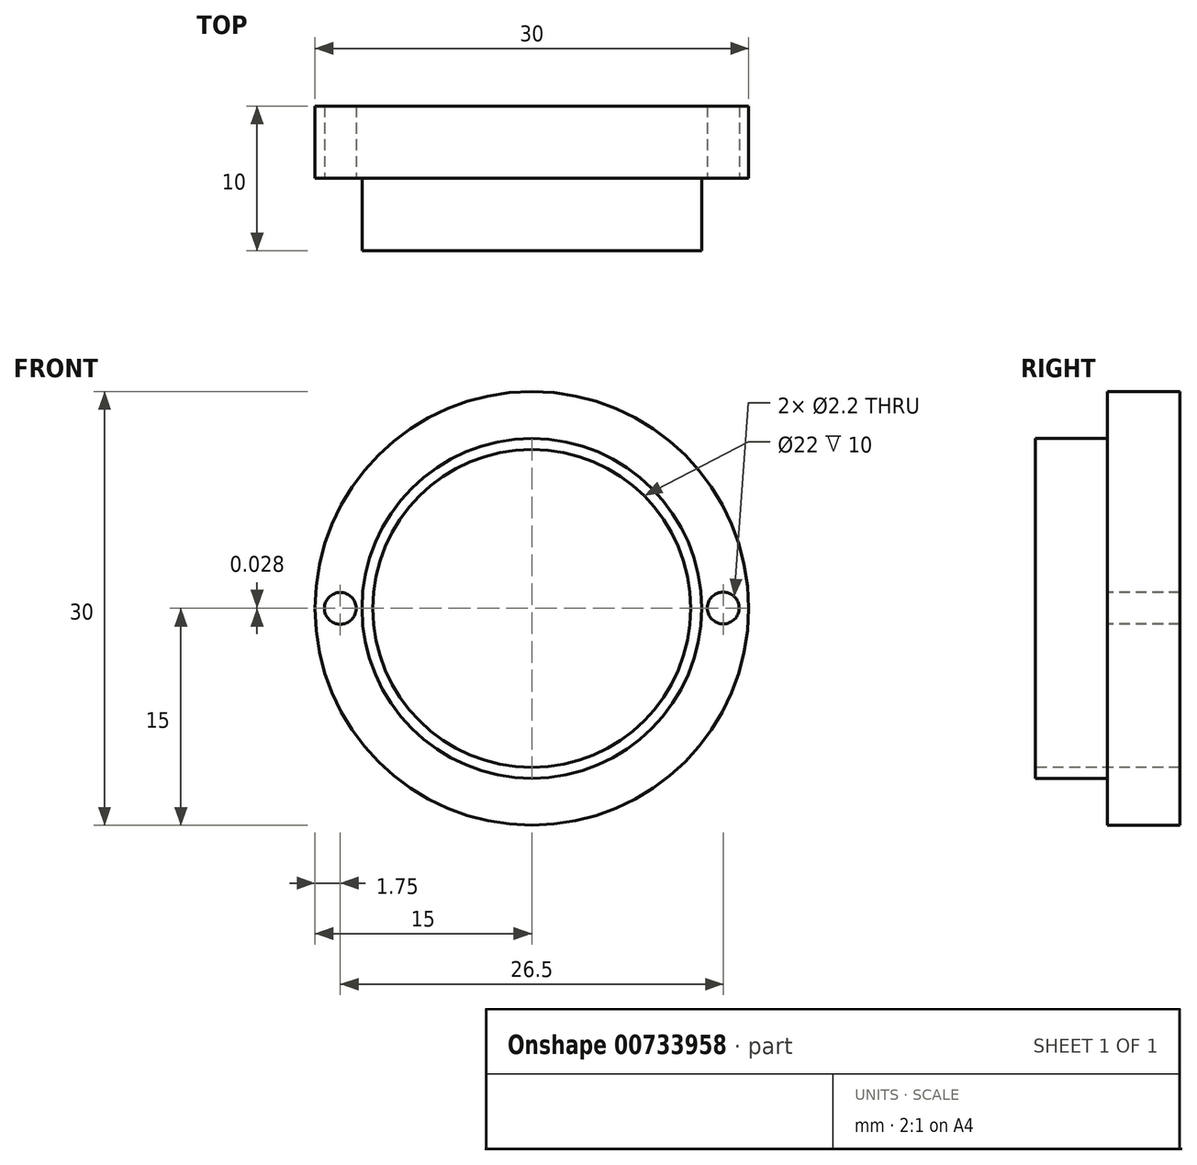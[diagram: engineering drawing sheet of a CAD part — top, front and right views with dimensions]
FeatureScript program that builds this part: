
annotation { "Feature Type Name" : "Feature", "Feature Type Description" : "" }
export const myFeature = defineFeature(function(context is Context, id is Id, definition is map)
    precondition{}
    {
        {
            var Q0;
            Q0=qCreatedBy(makeId("Front.planeOp"),FACE);
            var sketch = newSketch(context, id + "F0", { "sketchPlane" : qUnion([Q0])});
            skCircle(sketch, "E0", {"center": v(0, 0) * mm, "radius": 15 * mm});
            skSolve(sketch);
        }
        {
            var Q0;
            Q0=qCreatedBy(makeId("Front.planeOp"),FACE);
            var sketch = newSketch(context, id + "F1", { "sketchPlane" : qUnion([Q0])});
            skCircle(sketch, "E1", {"center": v(-13.25, 0) * mm, "radius": 1.1 * mm});
            skCircle(sketch, "E2", {"center": v(13.25, 0.03) * mm, "radius": 1.1 * mm});
            skSolve(sketch);
        }
        {
            var Q0;
            Q0=makeQuery(id+"F0.imprint","IMPRINT",FACE,{"disambiguationData":[TD([[makeQuery(id+"F0.imprint","IMPRINT",EDGE,{"derivedFrom":sQuery(id+"F0.wireOp",EDGE,"E0")}),1.0]])]});
            extrude(context, id + "F2", {"entities" : qUnion([Q0]), "oppositeDirection" : true, "depth" : 5 * mm, "offsetDistance" : 25 * mm});
        }
        {
            var Q0;
            Q0=makeQuery(id+"F1.imprint","IMPRINT",FACE,{"disambiguationData":[TD([[makeQuery(id+"F1.imprint","IMPRINT",EDGE,{"derivedFrom":sQuery(id+"F1.wireOp",EDGE,"E1")}),1.0]])]});
            var Q1;
            Q1=sQuery(id+"F1.wireOp",EDGE,"E1");
            extrude(context, id + "F3", {"entities" : qUnion([Q0]), "operationType" : NewBodyOperationType.REMOVE, "surfaceEntities" : qUnion([Q1]), "oppositeDirection" : true, "depth" : 5 * mm, "offsetDistance" : 25 * mm});
        }
        {
            var Q0;
            Q0 = qSketchRegion(id + "F1", true);
            extrude(context, id + "F4", {"entities" : qUnion([Q0]), "operationType" : NewBodyOperationType.REMOVE, "oppositeDirection" : true, "depth" : 5 * mm, "offsetDistance" : 25 * mm});
        }
        {
            var Q0;
            Q0=makeQuery(id+"F2.opExtrude","CAP_FACE",FACE,{"disambiguationData":[OSD([sQuery(id+"F0.wireOp",EDGE,"E0")])],"isStart":true});
            var sketch = newSketch(context, id + "F5", { "sketchPlane" : qUnion([Q0])});
            skCircle(sketch, "E3", {"center": v(0, 0) * mm, "radius": 11.75 * mm});
            skSolve(sketch);
        }
        {
            var Q0;
            Q0=makeQuery(id+"F5.imprint","IMPRINT",FACE,{"disambiguationData":[TD([[makeQuery(id+"F5.imprint","IMPRINT",EDGE,{"derivedFrom":sQuery(id+"F5.wireOp",EDGE,"E3")}),1.0]])]});
            var Q1;
            Q1=sQuery(id+"F5.wireOp",EDGE,"E3");
            extrude(context, id + "F6", {"entities" : qUnion([Q0]), "operationType" : NewBodyOperationType.ADD, "surfaceEntities" : qUnion([Q1]), "depth" : 5 * mm, "offsetDistance" : 25 * mm});
        }
        {
            var Q0;
            Q0=makeQuery(id+"F6.opExtrude","CAP_FACE",FACE,{"disambiguationData":[OSD([sQuery(id+"F5.wireOp",EDGE,"E3")])],"isStart":false});
            var sketch = newSketch(context, id + "F7", { "sketchPlane" : qUnion([Q0])});
            skCircle(sketch, "E4", {"center": v(0, 0) * mm, "radius": 11 * mm});
            skSolve(sketch);
        }
        {
            var Q0;
            Q0 = qSketchRegion(id + "F7", true);
            extrude(context, id + "F8", {"entities" : qUnion([Q0]), "operationType" : NewBodyOperationType.REMOVE, "oppositeDirection" : true, "depth" : 10 * mm, "offsetDistance" : 25 * mm});
        }
    });
